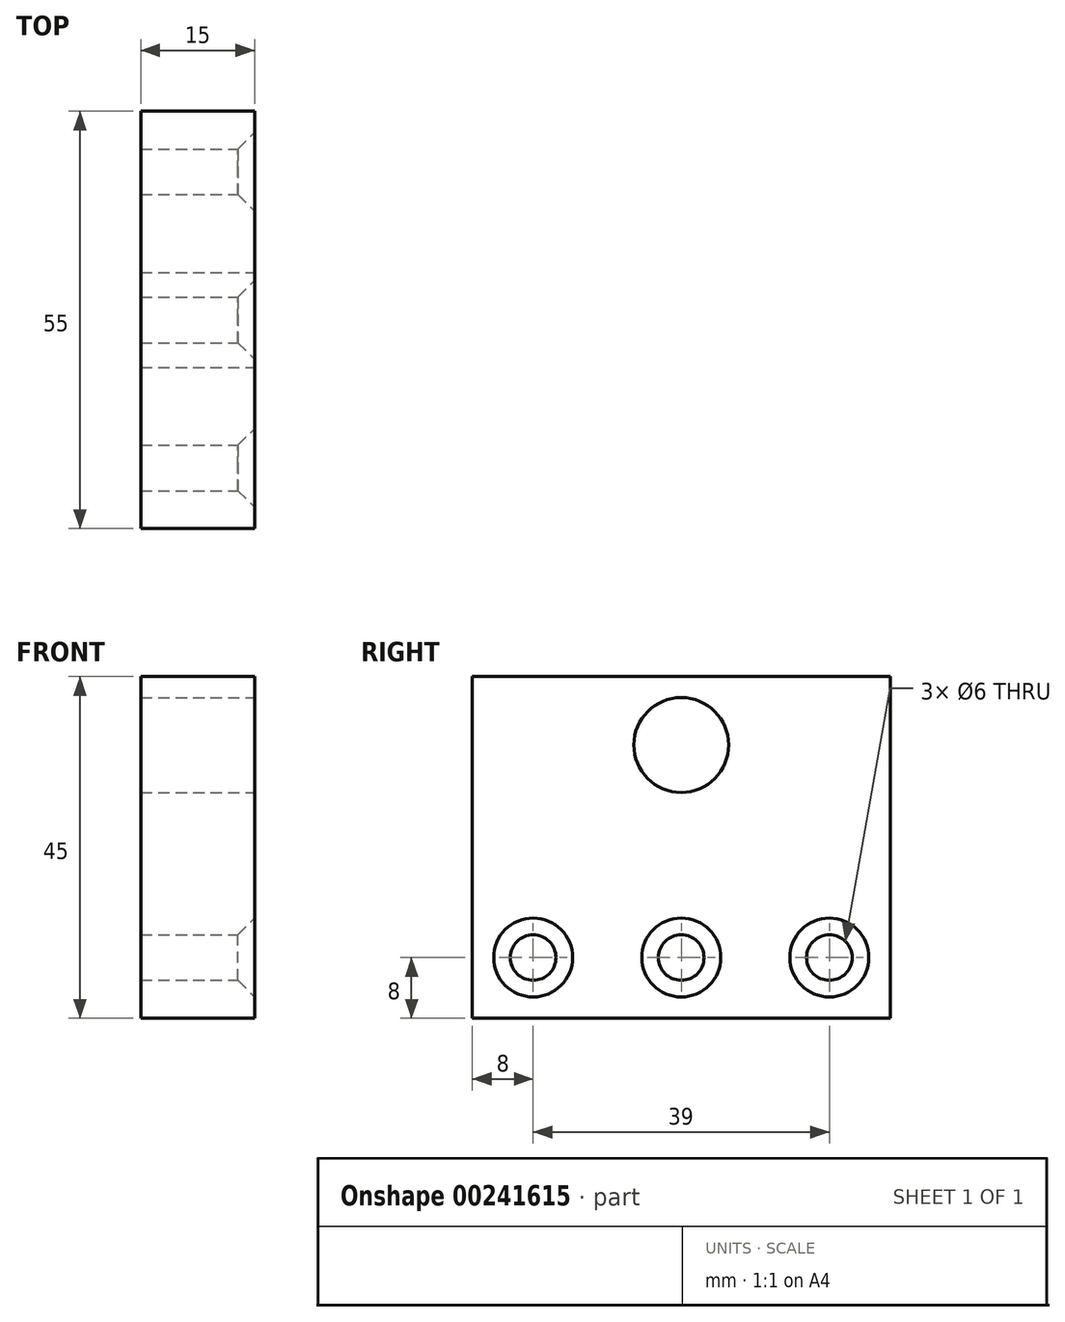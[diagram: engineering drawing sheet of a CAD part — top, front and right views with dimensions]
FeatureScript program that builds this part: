
annotation { "Feature Type Name" : "Feature", "Feature Type Description" : "" }
export const myFeature = defineFeature(function(context is Context, id is Id, definition is map)
    precondition{}
    {
        {
            var Q0;
            Q0=qCreatedBy(makeId("Right.planeOp"),FACE);
            var sketch = newSketch(context, id + "F0", { "sketchPlane" : qUnion([Q0])});
            skLineSegment(sketch, "E0.bottom", {"start": v(27.5, -22.5) * mm, "end": v(-27.5, -22.5) * mm});
            skLineSegment(sketch, "E0.top", {"start": v(27.5, 22.5) * mm, "end": v(-27.5, 22.5) * mm});
            skLineSegment(sketch, "E0.left", {"start": v(27.5, -22.5) * mm, "end": v(27.5, 22.5) * mm});
            skLineSegment(sketch, "E0.right", {"start": v(-27.5, -22.5) * mm, "end": v(-27.5, 22.5) * mm});
            skPoint(sketch, "E0.middle", {"position": v(0, 0) * mm});
            skSolve(sketch);
        }
        {
            var Q0;
            Q0 = qSketchRegion(id + "F0", true);
            extrude(context, id + "F1", {"entities" : qUnion([Q0]), "depth" : 15 * mm});
        }
        {
            var Q0;
            Q0=makeQuery(id+"F1.opExtrude","CAP_FACE",FACE,{"disambiguationData":[OSD([sQuery(id+"F0.wireOp",EDGE,"E0.bottom"),sQuery(id+"F0.wireOp",EDGE,"E0.top"),sQuery(id+"F0.wireOp",EDGE,"E0.left"),sQuery(id+"F0.wireOp",EDGE,"E0.right")])],"isStart":false});
            var sketch = newSketch(context, id + "F2", { "sketchPlane" : qUnion([Q0])});
            skPoint(sketch, "E1", {"position": v(0, 13.5) * mm});
            skPoint(sketch, "E2", {"position": v(-19.5, -14.5) * mm});
            skPoint(sketch, "E3", {"position": v(19.5, -14.5) * mm});
            skPoint(sketch, "E4", {"position": v(0, -14.5) * mm});
            skSolve(sketch);
        }
        {
            var Q0;
            Q0=sQuery(id+"F2.wireOp",VERTEX,"E1");
            var Q1;
            Q1=makeQuery(id+"F1.opExtrude","SWEPT_BODY",BODY,{"disambiguationData":[OSD([sQuery(id+"F0.wireOp",EDGE,"E0.bottom"),sQuery(id+"F0.wireOp",EDGE,"E0.top"),sQuery(id+"F0.wireOp",EDGE,"E0.left"),sQuery(id+"F0.wireOp",EDGE,"E0.right")])]});
            hole(context, id + "F3", {"style" : HoleStyle.SIMPLE, "endStyle" : HoleEndStyle.BLIND, "holeDiameter" : 12.5 * mm, "holeDepth" : 15 * mm, "startFromSketch" : true, "locations" : qUnion([Q0]), "scope" : qUnion([Q1])});
        }
        {
            var Q0;
            Q0=sQuery(id+"F2.wireOp",VERTEX,"E2");
            var Q1;
            Q1=sQuery(id+"F2.wireOp",VERTEX,"E4");
            var Q2;
            Q2=sQuery(id+"F2.wireOp",VERTEX,"E3");
            var Q3;
            Q3=makeQuery(id+"F1.opExtrude","SWEPT_BODY",BODY,{"disambiguationData":[OSD([sQuery(id+"F0.wireOp",EDGE,"E0.bottom"),sQuery(id+"F0.wireOp",EDGE,"E0.top"),sQuery(id+"F0.wireOp",EDGE,"E0.left"),sQuery(id+"F0.wireOp",EDGE,"E0.right")])]});
            hole(context, id + "F4", {"style" : HoleStyle.C_SINK, "endStyle" : HoleEndStyle.BLIND, "holeDiameter" : 6 * mm, "cSinkDiameter" : 10.4 * mm, "cSinkAngle" : 90 * degree, "holeDepth" : 15 * mm, "startFromSketch" : true, "locations" : qUnion([Q0, Q1, Q2]), "scope" : qUnion([Q3])});
        }
    });
